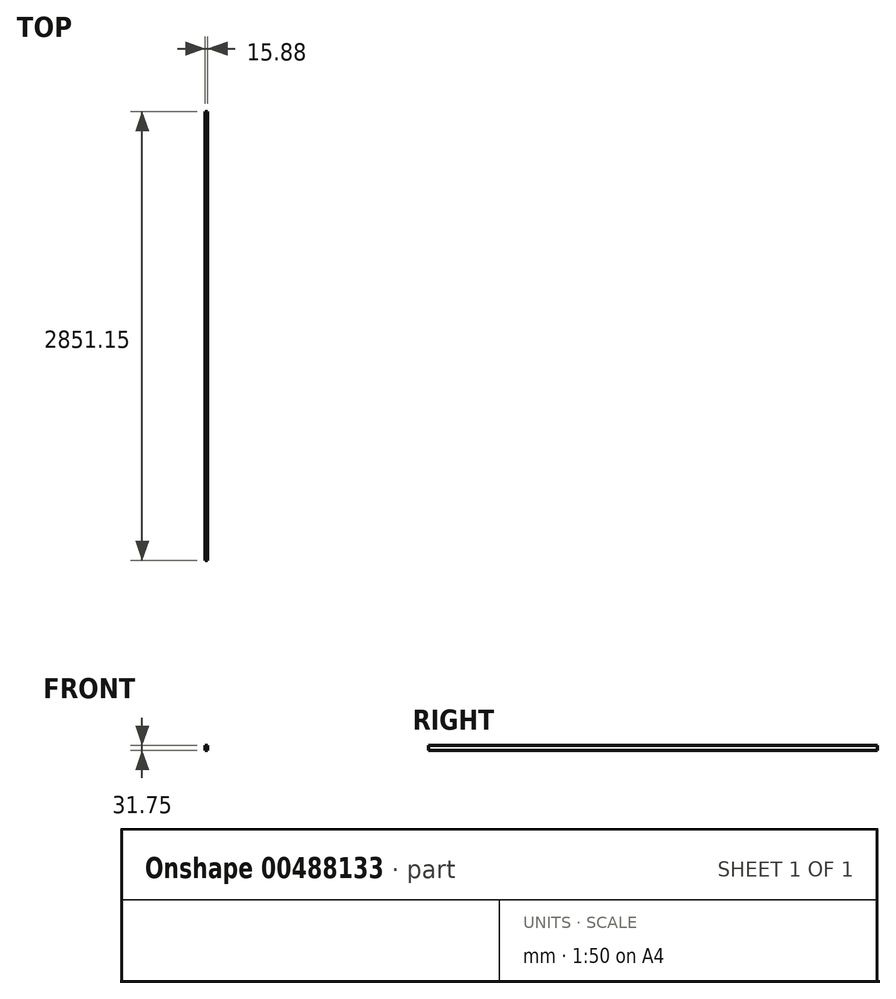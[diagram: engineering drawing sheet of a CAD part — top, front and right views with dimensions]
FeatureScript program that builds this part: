
annotation { "Feature Type Name" : "Feature", "Feature Type Description" : "" }
export const myFeature = defineFeature(function(context is Context, id is Id, definition is map)
    precondition{}
    {
        {
            var Q0;
            Q0=qCreatedBy(makeId("Front.planeOp"),FACE);
            var sketch = newSketch(context, id + "F0", { "sketchPlane" : qUnion([Q0])});
            skLineSegment(sketch, "E0", {"start": v(0, 0) * mm, "end": v(15.88, 0) * mm});
            skLineSegment(sketch, "E1", {"start": v(0, 0) * mm, "end": v(0, -31.75) * mm});
            skLineSegment(sketch, "E2", {"start": v(0, -31.75) * mm, "end": v(15.88, -31.75) * mm});
            skLineSegment(sketch, "E3", {"start": v(15.88, -31.75) * mm, "end": v(15.88, 0) * mm});
            skSolve(sketch);
        }
        {
            var Q0;
            Q0=makeQuery(id+"F0.imprint","IMPRINT",FACE,{"disambiguationData":[TD([[makeQuery(id+"F0.imprint","IMPRINT",EDGE,{"derivedFrom":sQuery(id+"F0.wireOp",EDGE,"E0")}),-1.0]])]});
            var Q1;
            Q1=makeQuery(id+"F0.imprint","IMPRINT",FACE,{"disambiguationData":[TD([[makeQuery(id+"F0.imprint","IMPRINT",EDGE,{"derivedFrom":sQuery(id+"F0.wireOp",EDGE,"E0")}),-1.0]])]});
            var Q2;
            Q2=makeQuery(id+"F0.imprint","IMPRINT",FACE,{"disambiguationData":[TD([[makeQuery(id+"F0.imprint","IMPRINT",EDGE,{"derivedFrom":sQuery(id+"F0.wireOp",EDGE,"sE00Gzr5-o4TN-UCdV-R85f-zcs0Y7AX2MqQ")}),1.0]])]});
            extrude(context, id + "F1", {"entities" : qUnion([Q0, Q1, Q2]), "oppositeDirection" : true, "depth" : 2870.2 * mm - 19.05 * mm, "offsetDistance" : 25.4 * mm});
        }
    });
